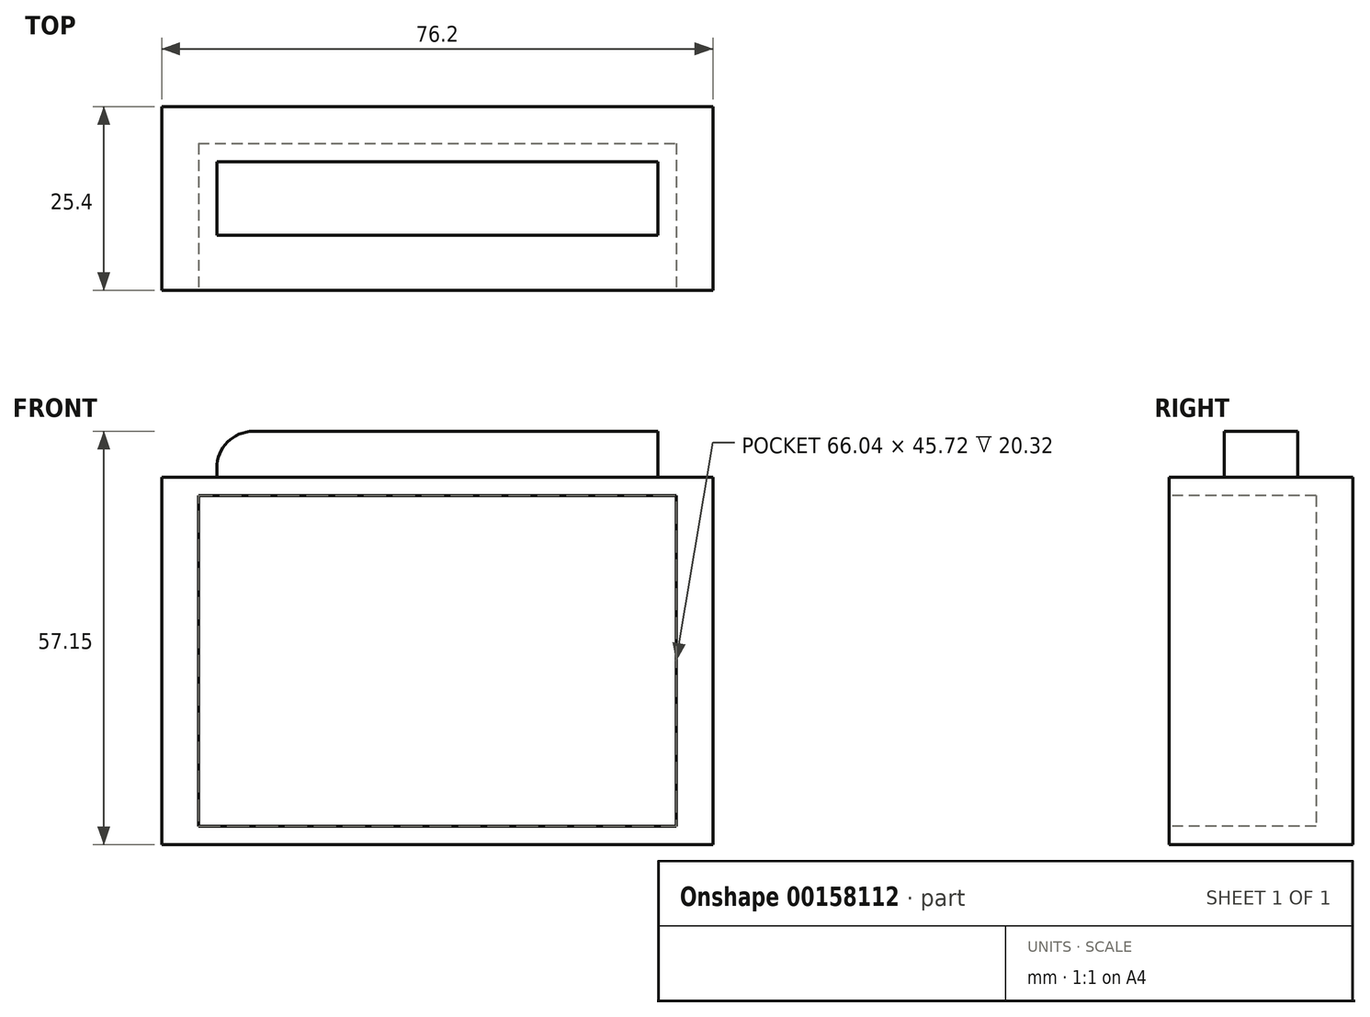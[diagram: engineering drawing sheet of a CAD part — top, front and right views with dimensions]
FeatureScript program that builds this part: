
annotation { "Feature Type Name" : "Feature", "Feature Type Description" : "" }
export const myFeature = defineFeature(function(context is Context, id is Id, definition is map)
    precondition{}
    {
        {
            var Q0;
            Q0=qCreatedBy(makeId("Front.planeOp"),FACE);
            var sketch = newSketch(context, id + "F0", { "sketchPlane" : qUnion([Q0])});
            skLineSegment(sketch, "E0.bottom", {"start": v(38.1, -25.4) * mm, "end": v(-38.1, -25.4) * mm});
            skLineSegment(sketch, "E0.top", {"start": v(38.1, 25.4) * mm, "end": v(-38.1, 25.4) * mm});
            skLineSegment(sketch, "E0.left", {"start": v(38.1, -25.4) * mm, "end": v(38.1, 25.4) * mm});
            skLineSegment(sketch, "E0.right", {"start": v(-38.1, -25.4) * mm, "end": v(-38.1, 25.4) * mm});
            skPoint(sketch, "E0.middle", {"position": v(0, 0) * mm});
            skSolve(sketch);
        }
        {
            var Q0;
            Q0 = qSketchRegion(id + "F0", true);
            extrude(context, id + "F1", {"entities" : qUnion([Q0]), "depth" : 25.4 * mm});
        }
        {
            var Q0;
            Q0=makeQuery(id+"F1.opExtrude","CAP_FACE",FACE,{"disambiguationData":[OSD([sQuery(id+"F0.wireOp",EDGE,"E0.bottom"),sQuery(id+"F0.wireOp",EDGE,"E0.top"),sQuery(id+"F0.wireOp",EDGE,"E0.left"),sQuery(id+"F0.wireOp",EDGE,"E0.right")])],"isStart":false});
            var sketch = newSketch(context, id + "F2", { "sketchPlane" : qUnion([Q0])});
            skLineSegment(sketch, "E1.bottom", {"start": v(-33.02, 22.86) * mm, "end": v(33.02, 22.86) * mm});
            skLineSegment(sketch, "E1.top", {"start": v(-33.02, -22.86) * mm, "end": v(33.02, -22.86) * mm});
            skLineSegment(sketch, "E1.left", {"start": v(-33.02, 22.86) * mm, "end": v(-33.02, -22.86) * mm});
            skLineSegment(sketch, "E1.right", {"start": v(33.02, 22.86) * mm, "end": v(33.02, -22.86) * mm});
            skSolve(sketch);
        }
        {
            var Q0;
            Q0 = qSketchRegion(id + "F2", true);
            var Q1;
            Q1=makeQuery(id+"F1.opExtrude","CAP_FACE",FACE,{"disambiguationData":[OSD([sQuery(id+"F0.wireOp",EDGE,"E0.bottom"),sQuery(id+"F0.wireOp",EDGE,"E0.top"),sQuery(id+"F0.wireOp",EDGE,"E0.left"),sQuery(id+"F0.wireOp",EDGE,"E0.right")])],"isStart":true});
            extrude(context, id + "F3", {"entities" : qUnion([Q0]), "operationType" : NewBodyOperationType.REMOVE, "oppositeDirection" : true, "endBoundEntityFace" : qUnion([Q1]), "depth" : 20.32 * mm, "hasSecondDirection" : true, "secondDirectionOppositeDirection" : false, "secondDirectionDepth" : 25.4 * mm});
        }
        {
            var Q0;
            Q0=makeQuery(id+"F1.opExtrude","SWEPT_FACE",FACE,{"disambiguationData":[OSD([sQuery(id+"F0.wireOp",EDGE,"E0.top")])]});
            var sketch = newSketch(context, id + "F4", { "sketchPlane" : qUnion([Q0])});
            skLineSegment(sketch, "E2.0", {"start": v(30.48, -7.62) * mm, "end": v(-30.48, -7.62) * mm});
            skLineSegment(sketch, "E2.1", {"start": v(30.48, -17.78) * mm, "end": v(30.48, -7.62) * mm});
            skLineSegment(sketch, "E2.2", {"start": v(-30.48, -17.78) * mm, "end": v(30.48, -17.78) * mm});
            skLineSegment(sketch, "E2.3", {"start": v(-30.48, -7.62) * mm, "end": v(-30.48, -17.78) * mm});
            skSolve(sketch);
        }
        {
            var Q0;
            Q0 = qSketchRegion(id + "F4", true);
            extrude(context, id + "F5", {"entities" : qUnion([Q0]), "operationType" : NewBodyOperationType.ADD, "depth" : 6.35 * mm});
        }
        {
            var Q0;
            Q0=makeQuery(id+"F5.opExtrude","CAP_EDGE",EDGE,{"disambiguationData":[OSD([sQuery(id+"F4.wireOp",EDGE,"E2.3")])],"isStart":false});
            fillet(context, id + "F6", {"entities" : qUnion([Q0]), "radius" : 5.08 * mm, "tangentPropagation" : true, "allowEdgeOverflow" : false});
        }
    });
